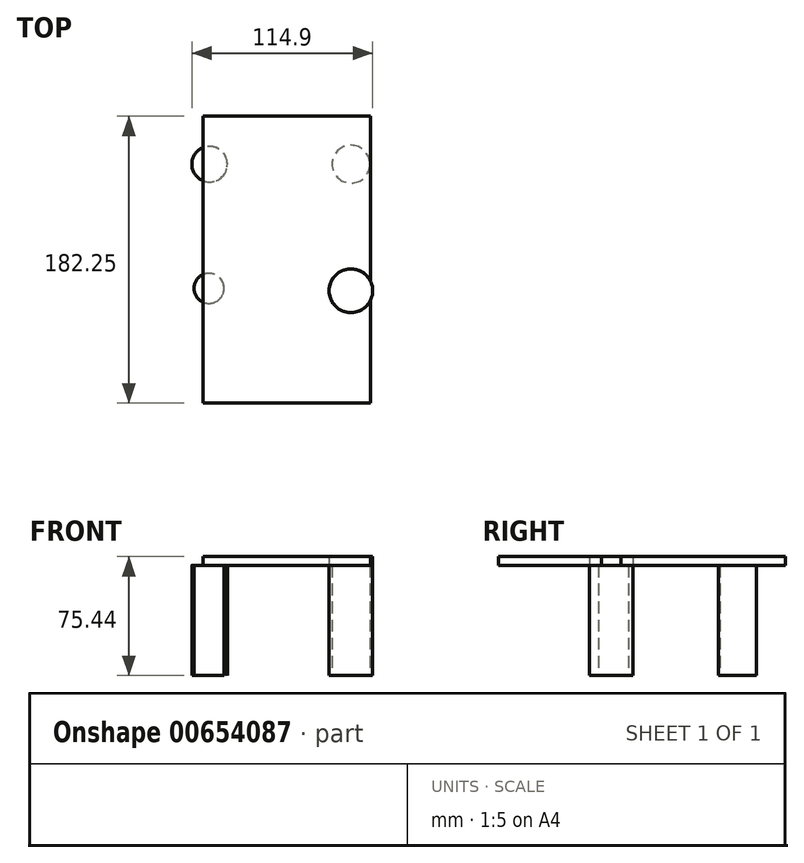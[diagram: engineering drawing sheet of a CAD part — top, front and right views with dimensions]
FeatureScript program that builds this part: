
annotation { "Feature Type Name" : "Feature", "Feature Type Description" : "" }
export const myFeature = defineFeature(function(context is Context, id is Id, definition is map)
    precondition{}
    {
        {
            var Q0;
            Q0=qCreatedBy(makeId("Top.planeOp"),FACE);
            var sketch = newSketch(context, id + "F0", { "sketchPlane" : qUnion([Q0])});
            skCircle(sketch, "E0", {"center": v(-61.4, -45.63) * mm, "radius": 9.57 * mm});
            skCircle(sketch, "E1", {"center": v(28.73, -47.13) * mm, "radius": 13.85 * mm});
            skCircle(sketch, "E2", {"center": v(28.73, 33.23) * mm, "radius": 12.04 * mm});
            skCircle(sketch, "E3", {"center": v(-61.02, 33.23) * mm, "radius": 11.3 * mm});
            skSolve(sketch);
        }
        {
            var Q0;
            Q0=makeQuery(id+"F0.imprint","IMPRINT",FACE,{"disambiguationData":[TD([[makeQuery(id+"F0.imprint","IMPRINT",EDGE,{"derivedFrom":sQuery(id+"F0.wireOp",EDGE,"E0")}),1.0]])]});
            var Q1;
            Q1=makeQuery(id+"F0.imprint","IMPRINT",FACE,{"disambiguationData":[TD([[makeQuery(id+"F0.imprint","IMPRINT",EDGE,{"derivedFrom":sQuery(id+"F0.wireOp",EDGE,"E3")}),1.0]])]});
            var Q2;
            Q2=makeQuery(id+"F0.imprint","IMPRINT",FACE,{"disambiguationData":[TD([[makeQuery(id+"F0.imprint","IMPRINT",EDGE,{"derivedFrom":sQuery(id+"F0.wireOp",EDGE,"E2")}),1.0]])]});
            var Q3;
            Q3=makeQuery(id+"F0.imprint","IMPRINT",FACE,{"disambiguationData":[TD([[makeQuery(id+"F0.imprint","IMPRINT",EDGE,{"derivedFrom":sQuery(id+"F0.wireOp",EDGE,"E1")}),1.0]])]});
            extrude(context, id + "F1", {"entities" : qUnion([Q0, Q1, Q2, Q3]), "depth" : 69.85 * mm, "offsetDistance" : 25.4 * mm});
        }
        {
            var Q0;
            Q0=makeQuery(id+"F1.opExtrude","CAP_FACE",FACE,{"disambiguationData":[OSD([sQuery(id+"F0.wireOp",EDGE,"E1")])],"isStart":false});
            var sketch = newSketch(context, id + "F2", { "sketchPlane" : qUnion([Q0])});
            skLineSegment(sketch, "E4.bottom", {"start": v(-65.14, 63.74) * mm, "end": v(41.14, 63.74) * mm});
            skLineSegment(sketch, "E4.top", {"start": v(-65.14, -118.5) * mm, "end": v(41.14, -118.5) * mm});
            skLineSegment(sketch, "E4.left", {"start": v(-65.14, 63.74) * mm, "end": v(-65.14, -118.5) * mm});
            skLineSegment(sketch, "E4.right", {"start": v(41.14, 63.74) * mm, "end": v(41.14, -118.5) * mm});
            skSolve(sketch);
        }
        {
            var Q0;
            Q0=makeQuery(id+"F1.opExtrude","CAP_FACE",FACE,{"disambiguationData":[OSD([sQuery(id+"F0.wireOp",EDGE,"E1")])],"isStart":false});
            var Q1;
            {var subQ1=sQuery(id+"F2.wireOp",EDGE,"E4.bottom");Q1=makeQuery(id+"F2.imprint","IMPRINT",FACE,{"disambiguationData":[TD([[makeQuery(id+"F2.imprint","IMPRINT",EDGE,{"derivedFrom":subQ1}),-1.0]])]});}
            extrude(context, id + "F3", {"entities" : qUnion([Q0, Q1]), "depth" : 5.6 * mm, "offsetDistance" : 25.4 * mm});
        }
    });
